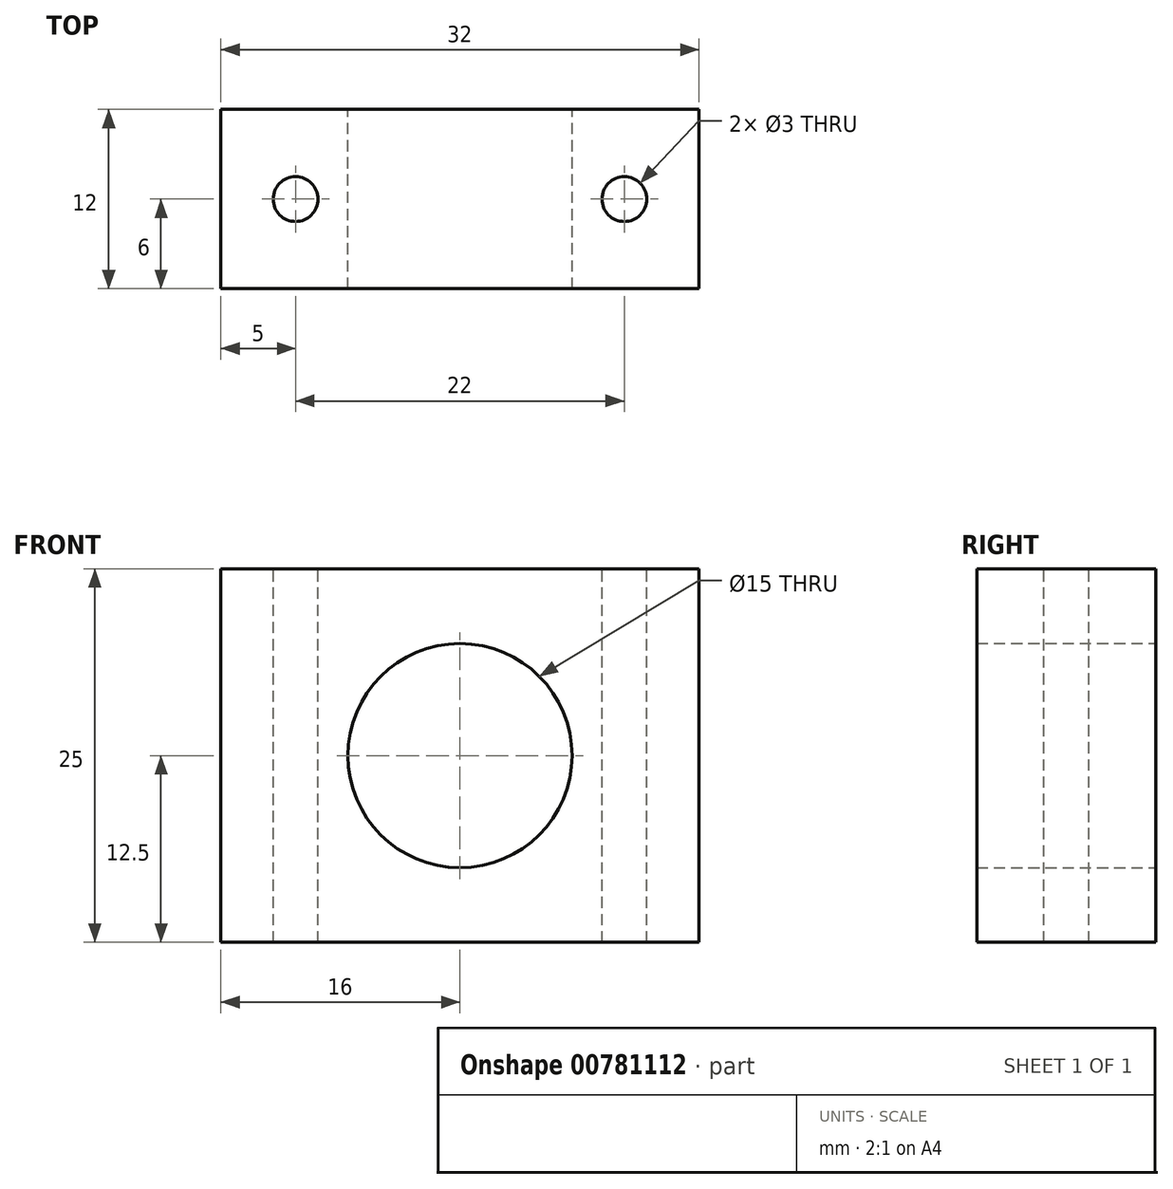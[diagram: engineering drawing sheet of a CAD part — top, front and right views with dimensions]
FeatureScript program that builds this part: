
annotation { "Feature Type Name" : "Feature", "Feature Type Description" : "" }
export const myFeature = defineFeature(function(context is Context, id is Id, definition is map)
    precondition{}
    {
        {
            var Q0;
            Q0=qCreatedBy(makeId("Front.planeOp"),FACE);
            var sketch = newSketch(context, id + "F0", { "sketchPlane" : qUnion([Q0])});
            skLineSegment(sketch, "E0.bottom", {"start": v(16, -12.5) * mm, "end": v(-16, -12.5) * mm});
            skLineSegment(sketch, "E0.top", {"start": v(16, 12.5) * mm, "end": v(-16, 12.5) * mm});
            skLineSegment(sketch, "E0.left", {"start": v(16, -12.5) * mm, "end": v(16, 12.5) * mm});
            skLineSegment(sketch, "E0.right", {"start": v(-16, -12.5) * mm, "end": v(-16, 12.5) * mm});
            skPoint(sketch, "E0.middle", {"position": v(0, 0) * mm});
            skCircle(sketch, "E1", {"center": v(0, 0) * mm, "radius": 7.5 * mm});
            skSolve(sketch);
        }
        {
            var Q0;
            Q0 = qSketchRegion(id + "F0", true);
            extrude(context, id + "F1", {"entities" : qUnion([Q0]), "endBound" : BoundingType.SYMMETRIC, "depth" : 12 * mm, "offsetDistance" : 25 * mm});
        }
        {
            var Q0;
            Q0=makeQuery(id+"F1.opExtrude","SWEPT_FACE",FACE,{"disambiguationData":[OSD([sQuery(id+"F0.wireOp",EDGE,"E0.top")])]});
            var sketch = newSketch(context, id + "F2", { "sketchPlane" : qUnion([Q0])});
            skLineSegment(sketch, "E2", {"start": v(-16, 0) * mm, "end": v(-11, 0) * mm, "construction": true});
            skLineSegment(sketch, "E3.MirrorCS", {"start": v(16, 0) * mm, "end": v(11, 0) * mm, "construction": true});
            skSolve(sketch);
        }
        {
            var Q0;
            Q0=sQuery(id+"F2.wireOp",VERTEX,"E2.end");
            var Q1;
            Q1=sQuery(id+"F2.wireOp",VERTEX,"E3.MirrorCS.end");
            var Q2;
            Q2=makeQuery(id+"F1.opExtrude","SWEPT_BODY",BODY,{"disambiguationData":[OSD([sQuery(id+"F0.wireOp",EDGE,"E0.bottom"),sQuery(id+"F0.wireOp",EDGE,"E0.top"),sQuery(id+"F0.wireOp",EDGE,"E0.left"),sQuery(id+"F0.wireOp",EDGE,"E0.right"),sQuery(id+"F0.wireOp",EDGE,"E1")])]});
            hole(context, id + "F3", {"style" : HoleStyle.SIMPLE, "endStyle" : HoleEndStyle.THROUGH, "holeDiameter" : 3 * mm, "majorDiameter" : 5 * mm, "isTappedThrough" : true, "tappedDepth" : 12 * mm, "tapClearance" : 3, "locations" : qUnion([Q0, Q1]), "scope" : qUnion([Q2])});
        }
    });
